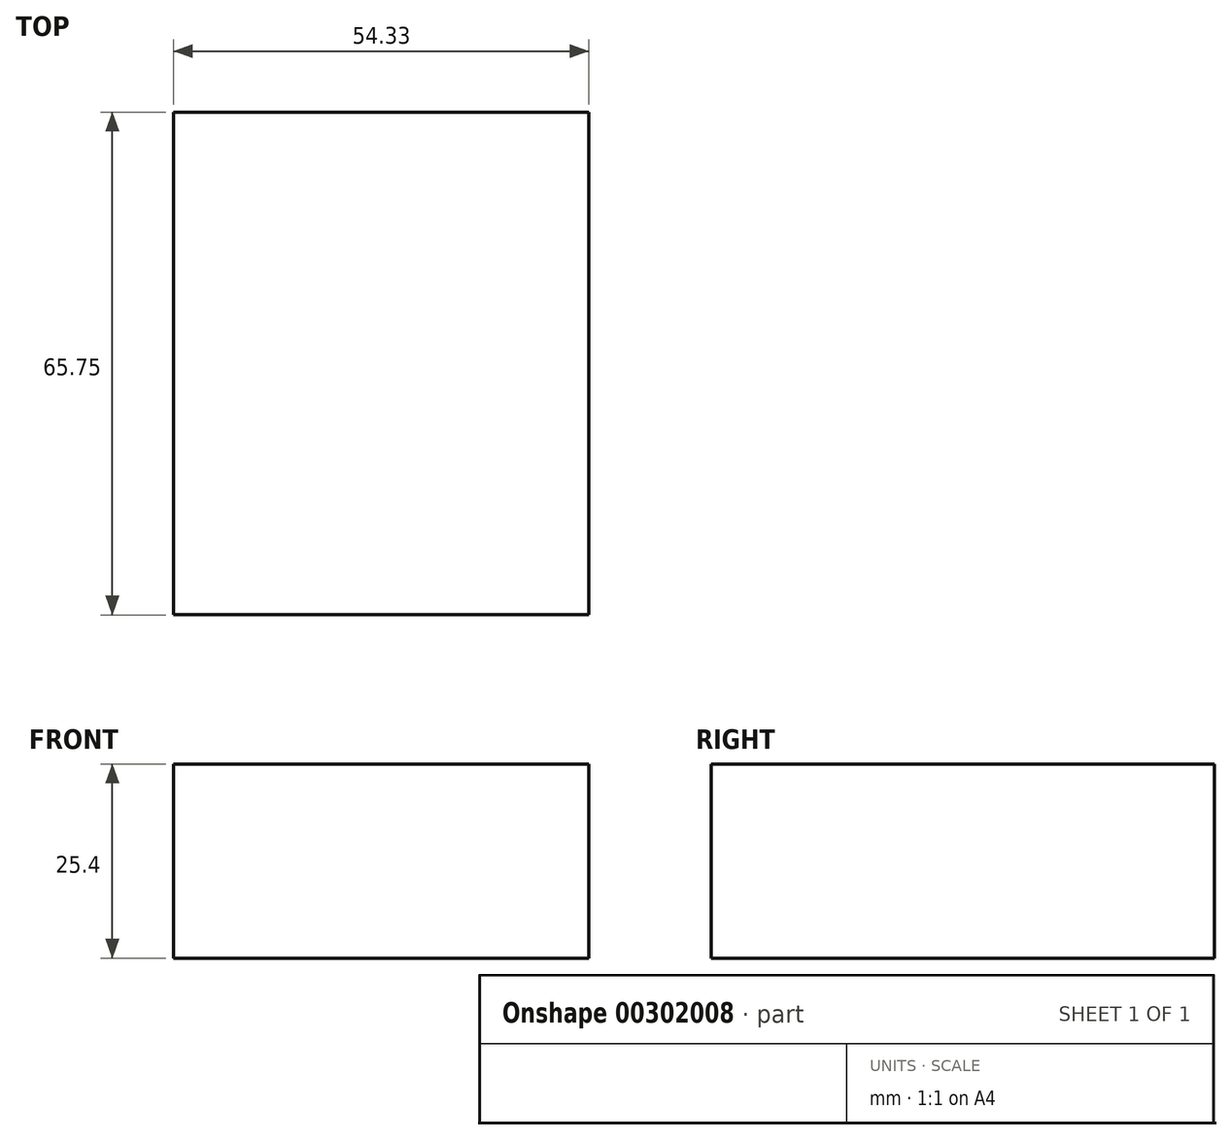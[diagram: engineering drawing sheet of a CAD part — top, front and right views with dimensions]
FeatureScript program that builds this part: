
annotation { "Feature Type Name" : "Feature", "Feature Type Description" : "" }
export const myFeature = defineFeature(function(context is Context, id is Id, definition is map)
    precondition{}
    {
        {
            var Q0;
            Q0=qCreatedBy(makeId("Top.planeOp"),FACE);
            var sketch = newSketch(context, id + "F0", { "sketchPlane" : qUnion([Q0])});
            skLineSegment(sketch, "E0.bottom", {"start": v(-107, 0) * mm, "end": v(-52.67, 0) * mm});
            skLineSegment(sketch, "E0.top", {"start": v(-107, -65.75) * mm, "end": v(-52.67, -65.75) * mm});
            skLineSegment(sketch, "E0.left", {"start": v(-107, 0) * mm, "end": v(-107, -65.75) * mm});
            skLineSegment(sketch, "E0.right", {"start": v(-52.67, 0) * mm, "end": v(-52.67, -65.75) * mm});
            skSolve(sketch);
        }
        {
            var Q0;
            Q0=makeQuery(id+"F0.imprint","IMPRINT",FACE,{"disambiguationData":[TD([[makeQuery(id+"F0.imprint","IMPRINT",EDGE,{"derivedFrom":sQuery(id+"F0.wireOp",EDGE,"E0.bottom")}),-1.0]])]});
            extrude(context, id + "F1", {"entities" : qUnion([Q0]), "depth" : 25.4 * mm, "offsetDistance" : 25.4 * mm});
        }
    });
